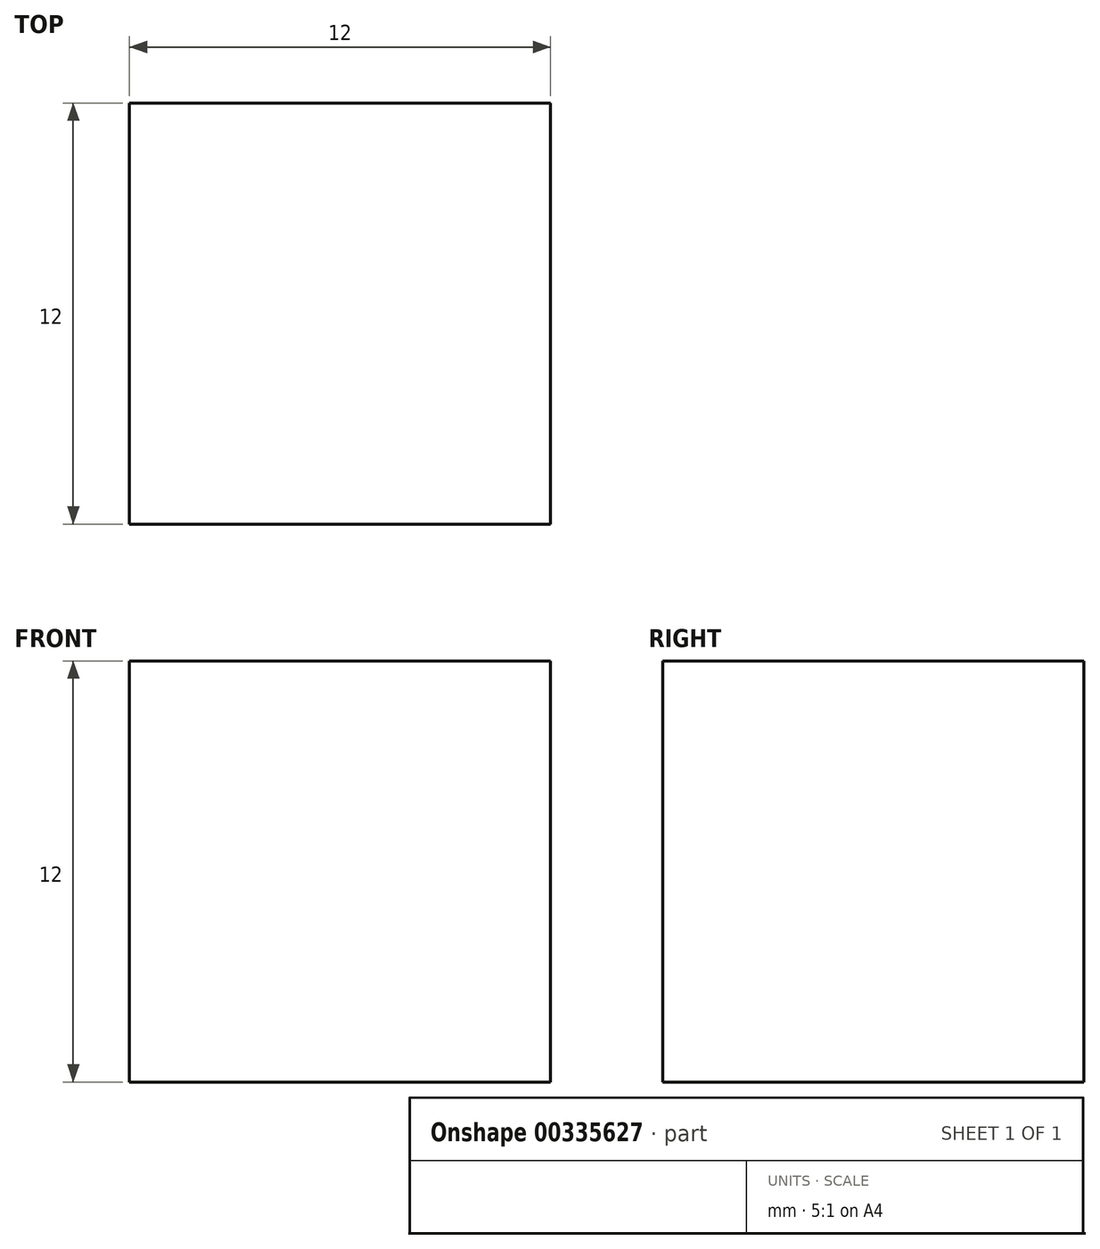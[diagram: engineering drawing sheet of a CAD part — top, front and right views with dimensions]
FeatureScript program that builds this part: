
annotation { "Feature Type Name" : "Feature", "Feature Type Description" : "" }
export const myFeature = defineFeature(function(context is Context, id is Id, definition is map)
    precondition{}
    {
        {
            var Q0;
            Q0=qCreatedBy(makeId("Top.planeOp"),FACE);
            var sketch = newSketch(context, id + "F0", { "sketchPlane" : qUnion([Q0])});
            skLineSegment(sketch, "E0.bottom", {"start": v(12, 12) * mm, "end": v(0, 12) * mm});
            skLineSegment(sketch, "E0.top", {"start": v(12, 0) * mm, "end": v(0, 0) * mm});
            skLineSegment(sketch, "E0.left", {"start": v(12, 12) * mm, "end": v(12, 0) * mm});
            skLineSegment(sketch, "E0.right", {"start": v(0, 12) * mm, "end": v(0, 0) * mm});
            skSolve(sketch);
        }
        {
            var Q0;
            Q0=makeQuery(id+"F0.imprint","IMPRINT",FACE,{"disambiguationData":[TD([[makeQuery(id+"F0.imprint","IMPRINT",EDGE,{"derivedFrom":sQuery(id+"F0.wireOp",EDGE,"E0.bottom")}),1.0]])]});
            extrude(context, id + "F1", {"entities" : qUnion([Q0]), "depth" : 12 * mm});
        }
    });
